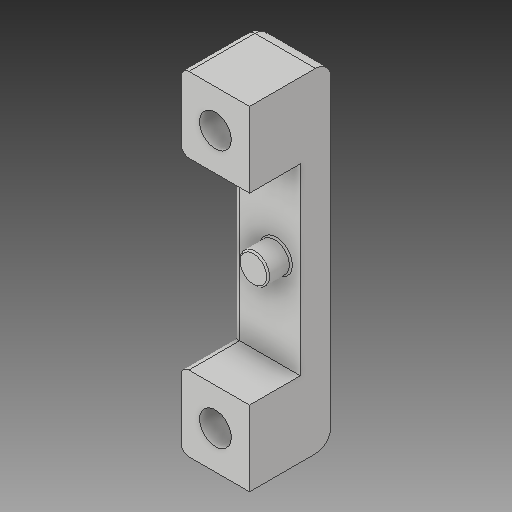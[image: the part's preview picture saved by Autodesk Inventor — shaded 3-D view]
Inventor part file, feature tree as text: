
AUTODESK INVENTOR PART (.ipt)
format: ipt  version: 2019 (Build 230136000, 136)  size: 148,480 bytes
history: native  units: mm
features: sketch x4, other x3
ambient origin geometry x8: Origin, YZ Plane, XZ Plane, XY Plane, X Axis, Y Axis, Z Axis, Center Point
bodies: Solid1 (feature_tree)
feature tree (7):
  other  "servo_cap.ipt"
  other  "Solid1::servo_cap.ipt"
  other  "TaggingFeature1"
  sketch  "Sketch1"  dims[d0=10.0mm]
  sketch  "Sketch2"
  sketch  "Sketch3"
  sketch  "Sketch4"
